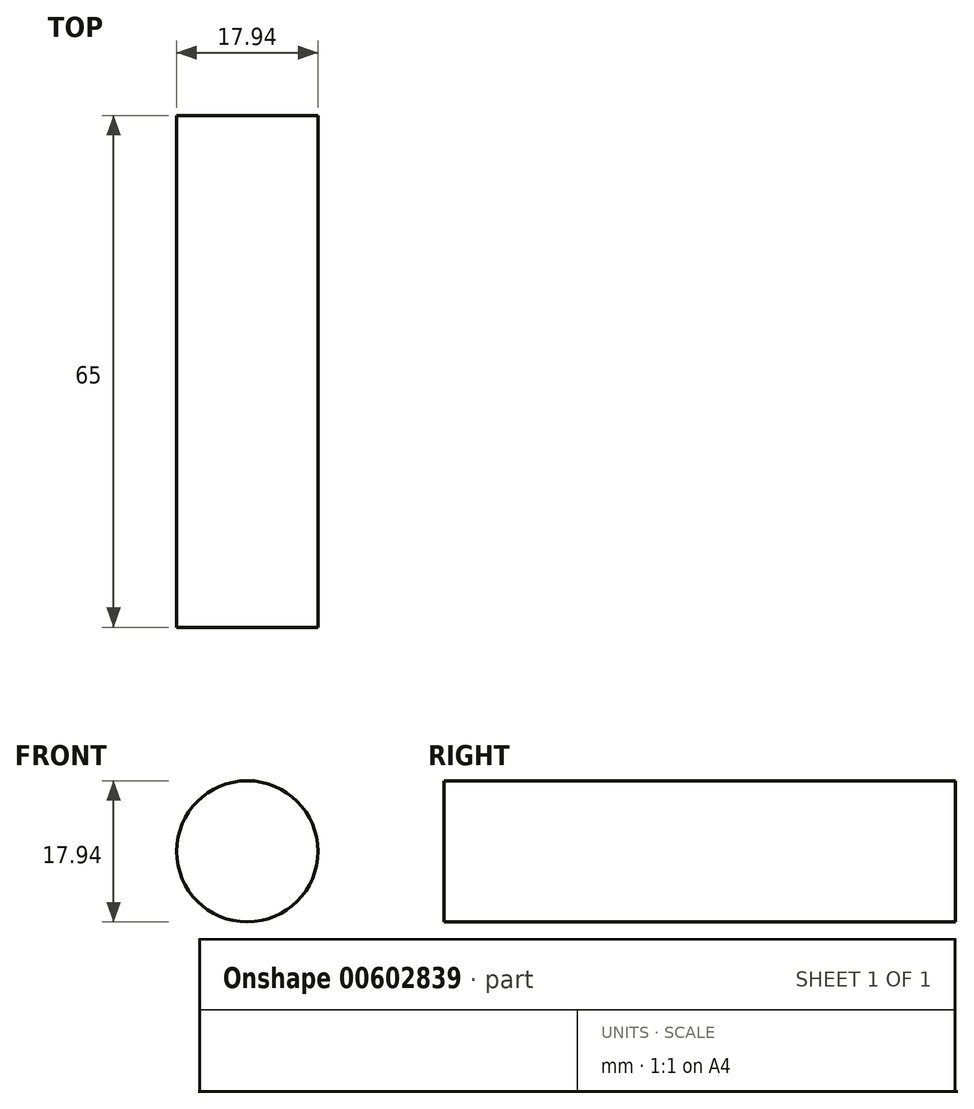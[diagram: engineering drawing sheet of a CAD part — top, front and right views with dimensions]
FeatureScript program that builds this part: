
annotation { "Feature Type Name" : "Feature", "Feature Type Description" : "" }
export const myFeature = defineFeature(function(context is Context, id is Id, definition is map)
    precondition{}
    {
        {
            var Q0;
            Q0=qCreatedBy(makeId("Front.planeOp"),FACE);
            var sketch = newSketch(context, id + "F0", { "sketchPlane" : qUnion([Q0])});
            skCircle(sketch, "E0", {"center": v(0, 0) * mm, "radius": 8.97 * mm});
            skSolve(sketch);
        }
        {
            var Q0;
            Q0=makeQuery(id+"F0.imprint","IMPRINT",FACE,{"disambiguationData":[TD([[makeQuery(id+"F0.imprint","IMPRINT",EDGE,{"derivedFrom":sQuery(id+"F0.wireOp",EDGE,"E0")}),1.0]])]});
            extrude(context, id + "F1", {"entities" : qUnion([Q0]), "depth" : 65 * mm, "offsetDistance" : 25 * mm});
        }
    });
